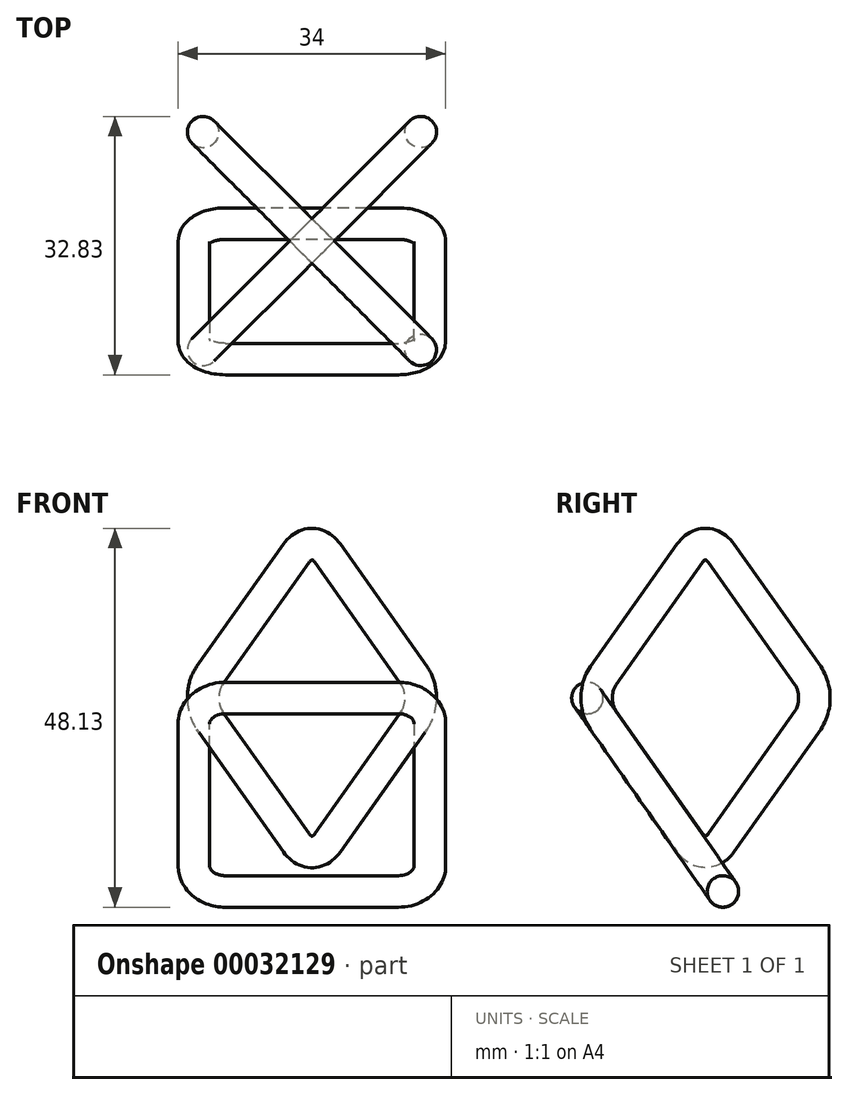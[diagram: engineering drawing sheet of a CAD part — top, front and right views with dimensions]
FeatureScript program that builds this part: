
annotation { "Feature Type Name" : "Feature", "Feature Type Description" : "" }
export const myFeature = defineFeature(function(context is Context, id is Id, definition is map)
    precondition{}
    {
        {
            var Q0;
            Q0=qCreatedBy(makeId("Top.planeOp"),FACE);
            var sketch = newSketch(context, id + "F0", { "sketchPlane" : qUnion([Q0])});
            skLineSegment(sketch, "E0", {"start": v(-15, -15) * mm, "end": v(0, 0) * mm});
            skLineSegment(sketch, "E1", {"start": v(0, 0) * mm, "end": v(15, 15) * mm});
            skLineSegment(sketch, "E2", {"start": v(-15, 15) * mm, "end": v(0, 0) * mm});
            skLineSegment(sketch, "E3", {"start": v(0, 0) * mm, "end": v(15, -15) * mm});
            skPoint(sketch, "E4.visualSharp", {"position": v(-15, -15) * mm});
            skArc(sketch, "E4.filletArc", {"start": v(-15, -11) * mm, "mid": v(-13.83, -13.83) * mm, "end": v(-11, -15) * mm});
            skPoint(sketch, "E5.visualSharp", {"position": v(15, -15) * mm});
            skArc(sketch, "E5.filletArc", {"start": v(11, -15) * mm, "mid": v(13.83, -13.83) * mm, "end": v(15, -11) * mm});
            skPoint(sketch, "E6.visualSharp", {"position": v(15, 15) * mm});
            skArc(sketch, "E6.filletArc", {"start": v(15, 11) * mm, "mid": v(13.83, 13.83) * mm, "end": v(11, 15) * mm});
            skPoint(sketch, "E7.visualSharp", {"position": v(-15, 15) * mm});
            skArc(sketch, "E7.filletArc", {"start": v(-11, 15) * mm, "mid": v(-13.83, 13.83) * mm, "end": v(-15, 11) * mm});
            skLineSegment(sketch, "E8", {"start": v(-11, 15) * mm, "end": v(0, 15) * mm});
            skLineSegment(sketch, "E9", {"start": v(0, 15) * mm, "end": v(11, 15) * mm});
            skLineSegment(sketch, "E10", {"start": v(15, 11) * mm, "end": v(15, 0) * mm});
            skLineSegment(sketch, "E11", {"start": v(15, 0) * mm, "end": v(15, -11) * mm});
            skLineSegment(sketch, "E12", {"start": v(11, -15) * mm, "end": v(0, -15) * mm});
            skLineSegment(sketch, "E13", {"start": v(0, -15) * mm, "end": v(-11, -15) * mm});
            skLineSegment(sketch, "E14", {"start": v(-15, -11) * mm, "end": v(-15, 0) * mm});
            skLineSegment(sketch, "E15", {"start": v(-15, 0) * mm, "end": v(-15, 11) * mm});
            skSolve(sketch);
        }
        {
            var Q0;
            Q0=qCreatedBy(makeId("Front.planeOp"),FACE);
            var sketch = newSketch(context, id + "F1", { "sketchPlane" : qUnion([Q0])});
            skPoint(sketch, "E16", {"position": v(0, 13.77) * mm});
            skPoint(sketch, "E17", {"position": v(0, -14.8) * mm});
            skLineSegment(sketch, "E18.0", {"start": v(-15, 0) * mm, "end": v(-11, 0) * mm});
            skCircle(sketch, "E19", {"center": v(-15, 0) * mm, "radius": 2 * mm});
            skLineSegment(sketch, "E20", {"start": v(0, -14.8) * mm, "end": v(0, 0) * mm});
            skLineSegment(sketch, "E21", {"start": v(0, 0) * mm, "end": v(0, 13.77) * mm});
            skSolve(sketch);
        }
        {
            var Q0;
            Q0=makeQuery(id+"F1.imprint","IMPRINT",FACE,{"disambiguationData":[TD([[makeQuery(id+"F1.imprint","IMPRINT",EDGE,{"derivedFrom":sQuery(id+"F1.wireOp",EDGE,"E19")}),1.0]])]});
            var Q1;
            Q1=sQuery(id+"F0.wireOp",EDGE,"E15");
            var Q2;
            Q2=sQuery(id+"F0.wireOp",EDGE,"E7.filletArc");
            var Q3;
            Q3=sQuery(id+"F0.wireOp",EDGE,"E8");
            var Q4;
            Q4=sQuery(id+"F0.wireOp",EDGE,"E9");
            var Q5;
            Q5=sQuery(id+"F0.wireOp",EDGE,"E6.filletArc");
            var Q6;
            Q6=sQuery(id+"F0.wireOp",EDGE,"E10");
            var Q7;
            Q7=sQuery(id+"F0.wireOp",EDGE,"E11");
            var Q8;
            Q8=sQuery(id+"F0.wireOp",EDGE,"E5.filletArc");
            var Q9;
            Q9=sQuery(id+"F0.wireOp",EDGE,"E12");
            var Q10;
            Q10=sQuery(id+"F0.wireOp",EDGE,"E13");
            var Q11;
            Q11=sQuery(id+"F0.wireOp",EDGE,"E4.filletArc");
            var Q12;
            Q12=sQuery(id+"F0.wireOp",EDGE,"E14");
            sweep(context, id + "F2", {"profiles" : qUnion([Q0]), "path" : qUnion([Q1, Q2, Q3, Q4, Q5, Q6, Q7, Q8, Q9, Q10, Q11, Q12])});
        }
        {
            var Q0;
            Q0=sQuery(id+"F0.wireOp",EDGE,"E0");
            var Q1;
            Q1=sQuery(id+"F0.wireOp",EDGE,"E2");
            extrude(context, id + "F3", {"bodyType" : ToolBodyType.SURFACE, "surfaceEntities" : qUnion([Q0, Q1]), "endBound" : BoundingType.SYMMETRIC, "depth" : 30 * mm});
        }
        {
            var Q0;
            Q0=makeQuery(id+"F2.opSweep","SWEPT_BODY",BODY,{"disambiguationData":[OSD([sQuery(id+"F0.wireOp",EDGE,"E14"),sQuery(id+"F1.wireOp",EDGE,"E19")])]});
            var Q1;
            Q1=sQuery(id+"F0.wireOp",EDGE,"E0");
            transform(context, id + "F4", {"entities" : qUnion([Q0]), "transformType" : TransformType.ROTATION, "transformAxis" : qUnion([Q1]), "angle" : 90 * degree, "makeCopy" : true});
        }
        {
            var Q0;
            Q0=makeQuery(id+"F4.opPattern","COPY",BODY,{"derivedFrom":makeQuery(id+"F2.opSweep","SWEPT_BODY",BODY,{"disambiguationData":[OSD([sQuery(id+"F0.wireOp",EDGE,"E14"),sQuery(id+"F1.wireOp",EDGE,"E19")])]}),"instanceName":"1"});
            var Q1;
            Q1=sQuery(id+"F1.wireOp",EDGE,"E21");
            transform(context, id + "F5", {"entities" : qUnion([Q0]), "transformType" : TransformType.ROTATION, "transformAxis" : qUnion([Q1]), "angle" : 90 * degree, "makeCopy" : true});
        }
        {
            var Q0;
            Q0=makeQuery(id+"F2.opSweep","SWEPT_BODY",BODY,{"disambiguationData":[OSD([sQuery(id+"F0.wireOp",EDGE,"E14"),sQuery(id+"F1.wireOp",EDGE,"E19")])]});
            var Q1;
            Q1=sQuery(id+"F0.wireOp",EDGE,"E13");
            transform(context, id + "F6", {"entities" : qUnion([Q0]), "transformType" : TransformType.ROTATION, "transformAxis" : qUnion([Q1]), "angle" : 55 * degree, "makeCopy" : false});
        }
    });
